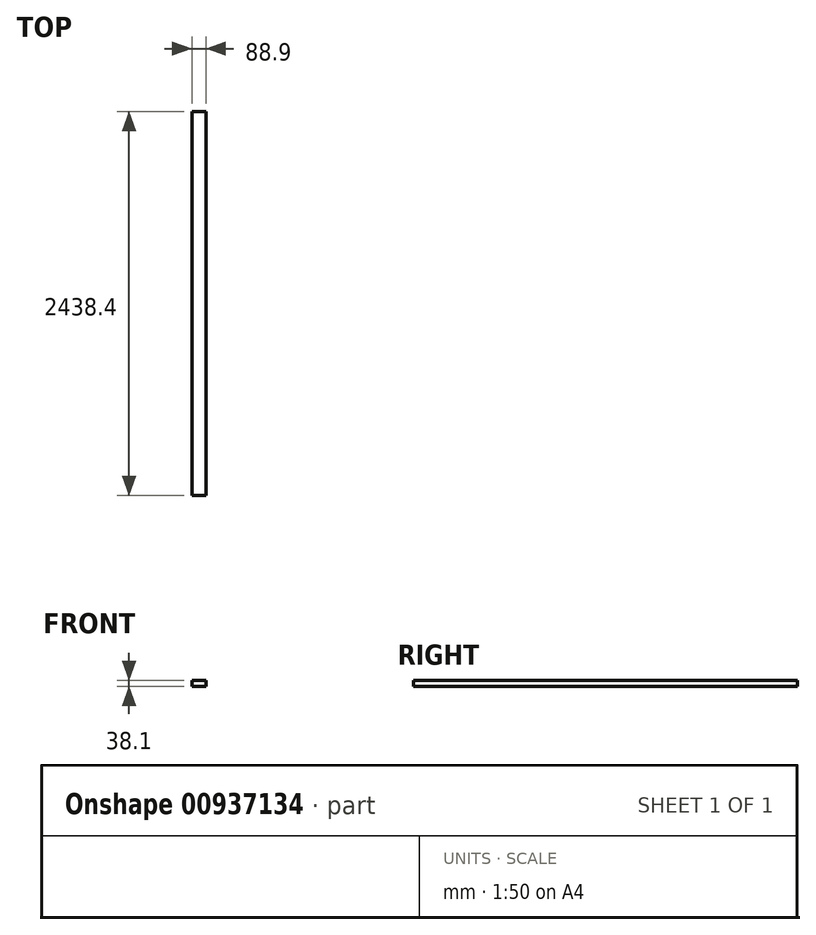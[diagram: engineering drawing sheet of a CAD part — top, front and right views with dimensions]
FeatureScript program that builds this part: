
annotation { "Feature Type Name" : "Feature", "Feature Type Description" : "" }
export const myFeature = defineFeature(function(context is Context, id is Id, definition is map)
    precondition{}
    {
        {
            var Q0;
            Q0=qCreatedBy(makeId("Front.planeOp"),FACE);
            var sketch = newSketch(context, id + "F0", { "sketchPlane" : qUnion([Q0])});
            skLineSegment(sketch, "E0.bottom", {"start": v(44.45, 19.05) * mm, "end": v(-44.45, 19.05) * mm});
            skLineSegment(sketch, "E0.top", {"start": v(44.45, -19.05) * mm, "end": v(-44.45, -19.05) * mm});
            skLineSegment(sketch, "E0.left", {"start": v(44.45, 19.05) * mm, "end": v(44.45, -19.05) * mm});
            skLineSegment(sketch, "E0.right", {"start": v(-44.45, 19.05) * mm, "end": v(-44.45, -19.05) * mm});
            skPoint(sketch, "E0.middle", {"position": v(0, 0) * mm});
            skSolve(sketch);
        }
        {
            var Q0;
            Q0 = qSketchRegion(id + "F0", true);
            extrude(context, id + "F1", {"entities" : qUnion([Q0]), "oppositeDirection" : true, "depth" : 2438.4 * mm, "offsetDistance" : 25.4 * mm});
        }
    });
